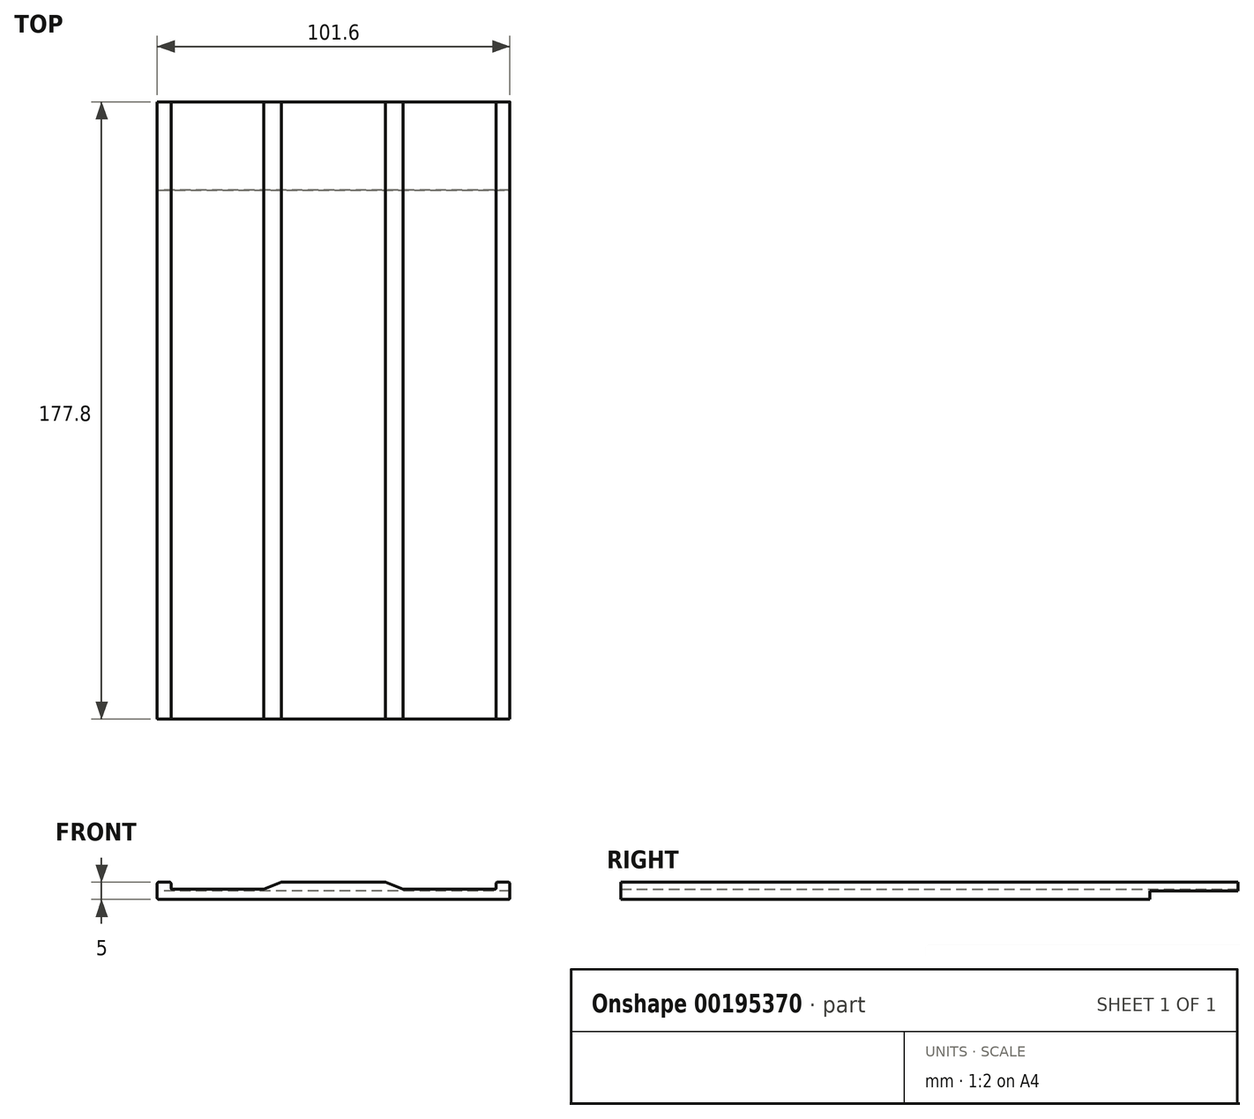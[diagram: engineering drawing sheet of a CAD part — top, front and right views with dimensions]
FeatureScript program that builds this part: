
annotation { "Feature Type Name" : "Feature", "Feature Type Description" : "" }
export const myFeature = defineFeature(function(context is Context, id is Id, definition is map)
    precondition{}
    {
        {
            var Q0;
            Q0=qCreatedBy(makeId("Front.planeOp"),FACE);
            var sketch = newSketch(context, id + "F0", { "sketchPlane" : qUnion([Q0])});
            skLineSegment(sketch, "E0.bottom", {"start": v(0.5, 0) * mm, "end": v(101.1, 0) * mm});
            skLineSegment(sketch, "E0.top", {"start": v(0.5, 5) * mm, "end": v(3.5, 5) * mm});
            skLineSegment(sketch, "E0.left", {"start": v(0, 0.5) * mm, "end": v(0, 4.5) * mm});
            skLineSegment(sketch, "E0.right", {"start": v(101.6, 0.5) * mm, "end": v(101.6, 4.5) * mm});
            skLineSegment(sketch, "E1.top", {"start": v(4.2, 3) * mm, "end": v(30.72, 3) * mm});
            skLineSegment(sketch, "E1.left", {"start": v(4, 4.5) * mm, "end": v(4, 3.2) * mm});
            skLineSegment(sketch, "E1.right", {"start": v(97.6, 4.5) * mm, "end": v(97.6, 3.2) * mm});
            skLineSegment(sketch, "E2.trimOffspring", {"start": v(98.1, 5) * mm, "end": v(101.1, 5) * mm});
            skPoint(sketch, "E3.visualSharp", {"position": v(0, 5) * mm});
            skArc(sketch, "E3.filletArc", {"start": v(0.5, 5) * mm, "mid": v(0.15, 4.85) * mm, "end": v(0, 4.5) * mm});
            skPoint(sketch, "E4.visualSharp", {"position": v(4, 5) * mm});
            skArc(sketch, "E4.filletArc", {"start": v(4, 4.5) * mm, "mid": v(3.85, 4.85) * mm, "end": v(3.5, 5) * mm});
            skPoint(sketch, "E5.visualSharp", {"position": v(4, 3) * mm});
            skArc(sketch, "E5.filletArc", {"start": v(4, 3.2) * mm, "mid": v(4.06, 3.06) * mm, "end": v(4.2, 3) * mm});
            skPoint(sketch, "E6.visualSharp", {"position": v(97.6, 3) * mm});
            skArc(sketch, "E6.filletArc", {"start": v(97.4, 3) * mm, "mid": v(97.54, 3.06) * mm, "end": v(97.6, 3.2) * mm});
            skPoint(sketch, "E7.visualSharp", {"position": v(97.6, 5) * mm});
            skArc(sketch, "E7.filletArc", {"start": v(98.1, 5) * mm, "mid": v(97.75, 4.85) * mm, "end": v(97.6, 4.5) * mm});
            skPoint(sketch, "E8.visualSharp", {"position": v(101.6, 5) * mm});
            skArc(sketch, "E8.filletArc", {"start": v(101.6, 4.5) * mm, "mid": v(101.45, 4.85) * mm, "end": v(101.1, 5) * mm});
            skPoint(sketch, "E9.visualSharp", {"position": v(101.6, 0) * mm});
            skArc(sketch, "E9.filletArc", {"start": v(101.1, 0) * mm, "mid": v(101.45, 0.15) * mm, "end": v(101.6, 0.5) * mm});
            skPoint(sketch, "E10.visualSharp", {"position": v(0, 0) * mm});
            skArc(sketch, "E10.filletArc", {"start": v(0, 0.5) * mm, "mid": v(0.15, 0.15) * mm, "end": v(0.5, 0) * mm});
            skLineSegment(sketch, "E11", {"start": v(35.8, 5) * mm, "end": v(65.8, 5) * mm});
            skLineSegment(sketch, "E12", {"start": v(65.8, 5) * mm, "end": v(70.88, 3) * mm});
            skLineSegment(sketch, "E13", {"start": v(35.8, 5) * mm, "end": v(30.72, 3) * mm});
            skLineSegment(sketch, "E14", {"start": v(50.8, 5) * mm, "end": v(50.8, 0) * mm, "construction": true});
            skLineSegment(sketch, "E15.trimOffspring", {"start": v(70.88, 3) * mm, "end": v(97.4, 3) * mm});
            skSolve(sketch);
        }
        {
            var Q0;
            Q0=qSketchRegion(id+"F0",true);
            extrude(context, id + "F1", {"entities" : qUnion([Q0]), "depth" : 177.8 * mm});
        }
        {
            var Q0;
            Q0=makeQuery(id+"F1.opExtrude","CAP_FACE",FACE,{"disambiguationData":[OSD([sQuery(id+"F0.wireOp",EDGE,"E0.bottom"),sQuery(id+"F0.wireOp",EDGE,"E0.top"),sQuery(id+"F0.wireOp",EDGE,"E0.left"),sQuery(id+"F0.wireOp",EDGE,"E0.right"),sQuery(id+"F0.wireOp",EDGE,"E1.top"),sQuery(id+"F0.wireOp",EDGE,"E1.left"),sQuery(id+"F0.wireOp",EDGE,"E1.right"),sQuery(id+"F0.wireOp",EDGE,"E2.trimOffspring"),sQuery(id+"F0.wireOp",EDGE,"E3.filletArc"),sQuery(id+"F0.wireOp",EDGE,"E4.filletArc"),sQuery(id+"F0.wireOp",EDGE,"E5.filletArc"),sQuery(id+"F0.wireOp",EDGE,"E6.filletArc"),sQuery(id+"F0.wireOp",EDGE,"E7.filletArc"),sQuery(id+"F0.wireOp",EDGE,"E8.filletArc"),sQuery(id+"F0.wireOp",EDGE,"E9.filletArc"),sQuery(id+"F0.wireOp",EDGE,"E10.filletArc"),sQuery(id+"F0.wireOp",EDGE,"E11"),sQuery(id+"F0.wireOp",EDGE,"E12"),sQuery(id+"F0.wireOp",EDGE,"E13"),sQuery(id+"F0.wireOp",EDGE,"E15.trimOffspring")])],"isStart":true});
            var sketch = newSketch(context, id + "F2", { "sketchPlane" : qUnion([Q0])});
            skLineSegment(sketch, "E16.bottom", {"start": v(-101.6, 5) * mm, "end": v(0, 5) * mm});
            skLineSegment(sketch, "E16.top", {"start": v(-101.6, 2.5) * mm, "end": v(0, 2.5) * mm});
            skLineSegment(sketch, "E16.left", {"start": v(-101.6, 5) * mm, "end": v(-101.6, 2.5) * mm});
            skLineSegment(sketch, "E16.right", {"start": v(0, 5) * mm, "end": v(0, 2.5) * mm});
            skLineSegment(sketch, "E17.top", {"start": v(-101.6, 0) * mm, "end": v(0, 0) * mm});
            skLineSegment(sketch, "E17.left", {"start": v(-101.6, 2.5) * mm, "end": v(-101.6, 0) * mm});
            skLineSegment(sketch, "E17.right", {"start": v(0, 2.5) * mm, "end": v(0, 0) * mm});
            skSolve(sketch);
        }
        {
            var Q0;
            {var subQ2=sQuery(id+"F2.wireOp",EDGE,"E16.top");Q0=makeQuery(id+"F2.imprint","IMPRINT",FACE,{"disambiguationData":[TD([[makeQuery(id+"F2.imprint","IMPRINT",EDGE,{"derivedFrom":subQ2}),-1.0]])]});}
            extrude(context, id + "F3", {"entities" : qUnion([Q0]), "operationType" : NewBodyOperationType.REMOVE, "oppositeDirection" : true, "depth" : 25.4 * mm});
        }
    });
